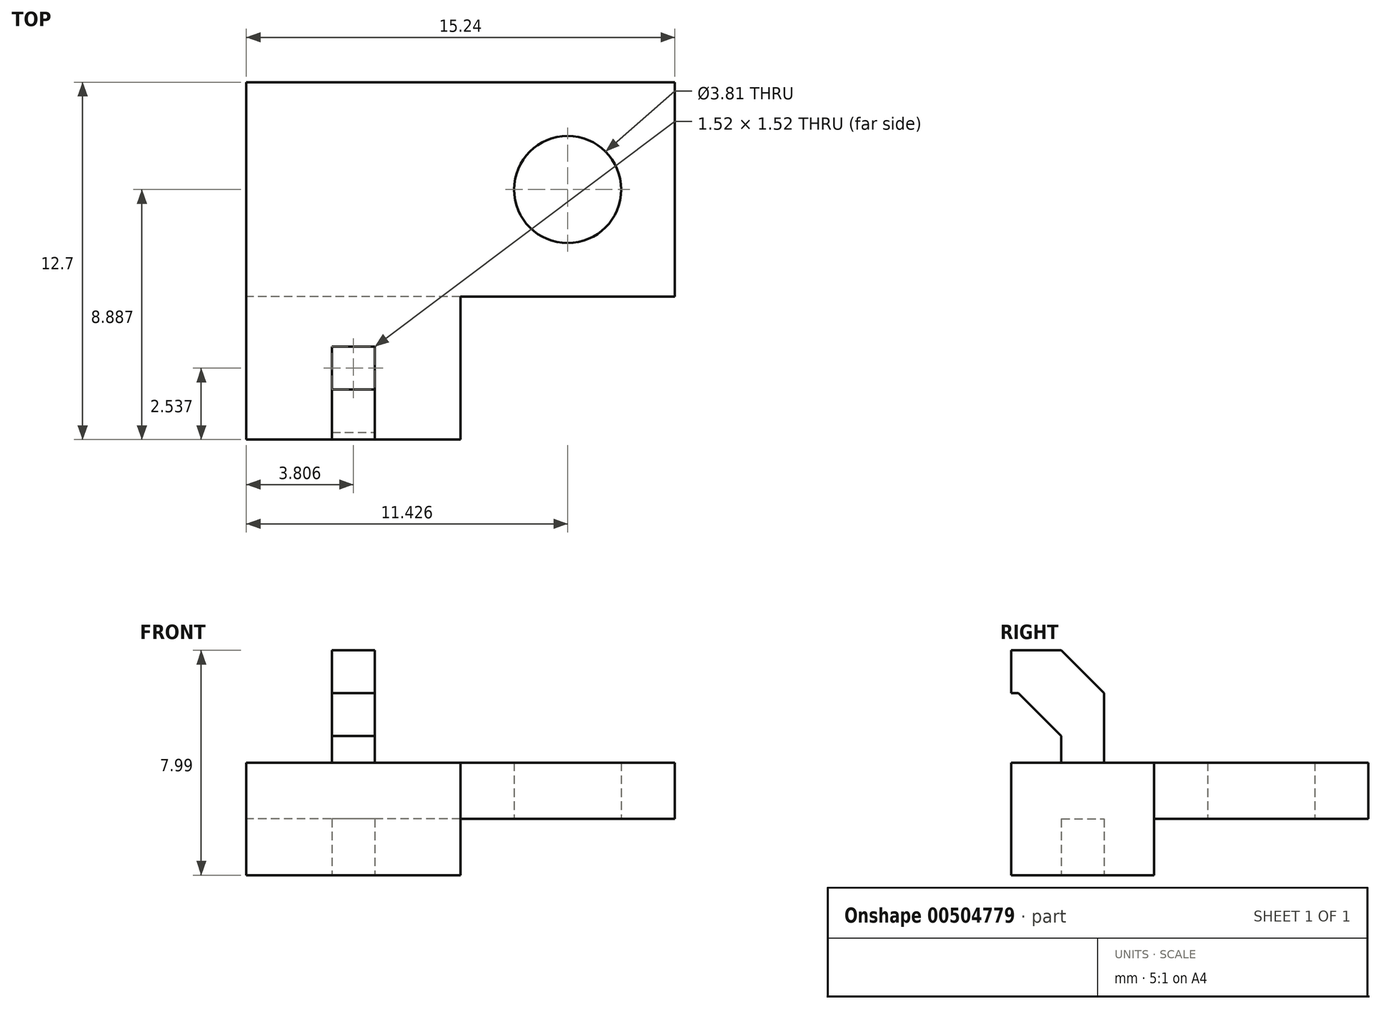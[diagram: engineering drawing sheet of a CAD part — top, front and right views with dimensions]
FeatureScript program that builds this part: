
annotation { "Feature Type Name" : "Feature", "Feature Type Description" : "" }
export const myFeature = defineFeature(function(context is Context, id is Id, definition is map)
    precondition{}
    {
        {
            var Q0;
            Q0=qCreatedBy(makeId("Top.planeOp"),FACE);
            var sketch = newSketch(context, id + "F0", { "sketchPlane" : qUnion([Q0])});
            skLineSegment(sketch, "E0", {"start": v(-32.48, 5.1) * mm, "end": v(-47.72, 5.1) * mm});
            skLineSegment(sketch, "E1", {"start": v(-47.72, 5.1) * mm, "end": v(-47.72, -7.6) * mm});
            skLineSegment(sketch, "E2", {"start": v(-47.72, -7.6) * mm, "end": v(-40.1, -7.6) * mm});
            skLineSegment(sketch, "E3", {"start": v(-40.1, -7.6) * mm, "end": v(-40.1, -2.52) * mm});
            skLineSegment(sketch, "E4", {"start": v(-40.1, -2.52) * mm, "end": v(-32.48, -2.52) * mm});
            skLineSegment(sketch, "E5", {"start": v(-32.48, -2.52) * mm, "end": v(-32.48, 5.1) * mm});
            skLineSegment(sketch, "E6", {"start": v(-40.1, -2.52) * mm, "end": v(-47.72, -2.52) * mm});
            skPoint(sketch, "E7", {"position": v(-43.91, -2.52) * mm});
            skPoint(sketch, "E8", {"position": v(-40.1, -5.06) * mm});
            skPoint(sketch, "E9", {"position": v(-36.3, -2.52) * mm});
            skPoint(sketch, "E10", {"position": v(-32.48, 1.29) * mm});
            skCircle(sketch, "E11", {"center": v(-36.3, 1.29) * mm, "radius": 1.9 * mm});
            skLineSegment(sketch, "E12.bottom", {"start": v(-43.15, -5.82) * mm, "end": v(-44.68, -5.82) * mm});
            skLineSegment(sketch, "E12.top", {"start": v(-43.15, -4.3) * mm, "end": v(-44.68, -4.3) * mm});
            skLineSegment(sketch, "E12.left", {"start": v(-43.15, -5.82) * mm, "end": v(-43.15, -4.3) * mm});
            skLineSegment(sketch, "E12.right", {"start": v(-44.68, -5.82) * mm, "end": v(-44.68, -4.3) * mm});
            skPoint(sketch, "E12.middle", {"position": v(-43.91, -5.06) * mm});
            skSolve(sketch);
        }
        {
            var Q0;
            {var subQ1=sQuery(id+"F0.wireOp",EDGE,"E0");Q0=makeQuery(id+"F0.imprint","IMPRINT",FACE,{"disambiguationData":[TD([[makeQuery(id+"F0.imprint","IMPRINT",EDGE,{"derivedFrom":subQ1}),1.0]])]});}
            var Q1;
            {var subQ0=sQuery(id+"F0.wireOp",EDGE,"E2");Q1=makeQuery(id+"F0.imprint","IMPRINT",FACE,{"disambiguationData":[TD([[makeQuery(id+"F0.imprint","IMPRINT",EDGE,{"derivedFrom":subQ0}),1.0]])]});}
            var Q2;
            Q2=makeQuery(id+"F0.imprint","IMPRINT",FACE,{"disambiguationData":[TD([[makeQuery(id+"F0.imprint","IMPRINT",EDGE,{"derivedFrom":sQuery(id+"F0.wireOp",EDGE,"ck5qkCs0-l2rh-cVaE-YExQ-hsTsS1hAtag5")}),1.0]])]});
            extrude(context, id + "F1", {"entities" : qUnion([Q0, Q1, Q2]), "depth" : 2 * mm, "offsetDistance" : 25.4 * mm});
        }
        {
            var Q0;
            {var subQ0=sQuery(id+"F0.wireOp",EDGE,"E2");Q0=makeQuery(id+"F0.imprint","IMPRINT",FACE,{"disambiguationData":[TD([[makeQuery(id+"F0.imprint","IMPRINT",EDGE,{"derivedFrom":subQ0}),1.0]])]});}
            var Q1;
            Q1=makeQuery(id+"F0.imprint","IMPRINT",FACE,{"disambiguationData":[TD([[makeQuery(id+"F0.imprint","IMPRINT",EDGE,{"derivedFrom":sQuery(id+"F0.wireOp",EDGE,"ck5qkCs0-l2rh-cVaE-YExQ-hsTsS1hAtag5")}),1.0]])]});
            extrude(context, id + "F2", {"entities" : qUnion([Q0, Q1]), "operationType" : NewBodyOperationType.ADD, "oppositeDirection" : true, "depth" : 2 * mm, "offsetDistance" : 25.4 * mm});
        }
        {
            var Q0;
            Q0=makeQuery(id+"F0.imprint","IMPRINT",FACE,{"disambiguationData":[TD([[makeQuery(id+"F0.imprint","IMPRINT",EDGE,{"derivedFrom":sQuery(id+"F0.wireOp",EDGE,"E12.bottom")}),-1.0]])]});
            extrude(context, id + "F3", {"entities" : qUnion([Q0]), "operationType" : NewBodyOperationType.ADD, "depth" : 6 * mm, "offsetDistance" : 25.4 * mm});
        }
        {
            var Q0;
            {var subQ0=sQuery(id+"F0.wireOp",EDGE,"E2");Q0=makeQuery(id+"F2.boolean.opBoolean","MERGE",FACE,{"derivedFrom":[makeQuery(id+"F1.opExtrude","SWEPT_FACE",FACE,{"disambiguationData":[OSD([subQ0])]}),makeQuery(id+"F2.opExtrude","SWEPT_FACE",FACE,{"disambiguationData":[OSD([subQ0])]})]});}
            var sketch = newSketch(context, id + "F4", { "sketchPlane" : qUnion([Q0])});
            skLineSegment(sketch, "E13", {"start": v(-44.68, 2) * mm, "end": v(-44.68, 6) * mm});
            skLineSegment(sketch, "E14", {"start": v(-43.15, 6) * mm, "end": v(-43.15, 2) * mm});
            skLineSegment(sketch, "E15", {"start": v(-44.68, 4.47) * mm, "end": v(-43.15, 4.47) * mm});
            skLineSegment(sketch, "E16", {"start": v(-44.68, 6) * mm, "end": v(-43.15, 6) * mm});
            skLineSegment(sketch, "E17.0.0", {"start": v(-44.68, 2) * mm, "end": v(-43.15, 2) * mm});
            skLineSegment(sketch, "E17.0.1", {"start": v(-43.15, 2) * mm, "end": v(-43.15, 6) * mm});
            skLineSegment(sketch, "E17.0.2", {"start": v(-43.15, 6) * mm, "end": v(-44.68, 6) * mm});
            skLineSegment(sketch, "E17.0.3", {"start": v(-44.68, 6) * mm, "end": v(-44.68, 2) * mm});
            skPoint(sketch, "E18", {"position": v(-43.91, 6) * mm});
            skSolve(sketch);
        }
        {
            var Q0;
            {var subQ2=sQuery(id+"F4.wireOp",EDGE,"E15");Q0=makeQuery(id+"F4.imprint","IMPRINT",FACE,{"disambiguationData":[TD([[makeQuery(id+"F4.imprint","IMPRINT",EDGE,{"derivedFrom":subQ2}),1.0]])]});}
            extrude(context, id + "F5", {"entities" : qUnion([Q0]), "operationType" : NewBodyOperationType.ADD, "oppositeDirection" : true, "depth" : 2.46 * mm, "offsetDistance" : 25.4 * mm});
        }
        {
            var Q0;
            Q0=makeQuery(id+"F5.boolean.opBoolean","INTERSECT",EDGE,{"derivedFrom":[makeQuery(id+"F3.opExtrude","SWEPT_FACE",FACE,{"disambiguationData":[OSD([sQuery(id+"F0.wireOp",EDGE,"E12.bottom")])]}),makeQuery(id+"F5.opExtrude","SWEPT_FACE",FACE,{"disambiguationData":[OSD([sQuery(id+"F4.wireOp",EDGE,"E15")])]})]});
            var Q1;
            Q1=makeQuery(id+"F3.opExtrude","CAP_EDGE",EDGE,{"disambiguationData":[OSD([sQuery(id+"F0.wireOp",EDGE,"E12.top")])],"isStart":false});
            chamfer(context, id + "F6", {"entities" : qUnion([Q0, Q1]), "width" : 1.52 * mm, "tangentPropagation" : true});
        }
    });
